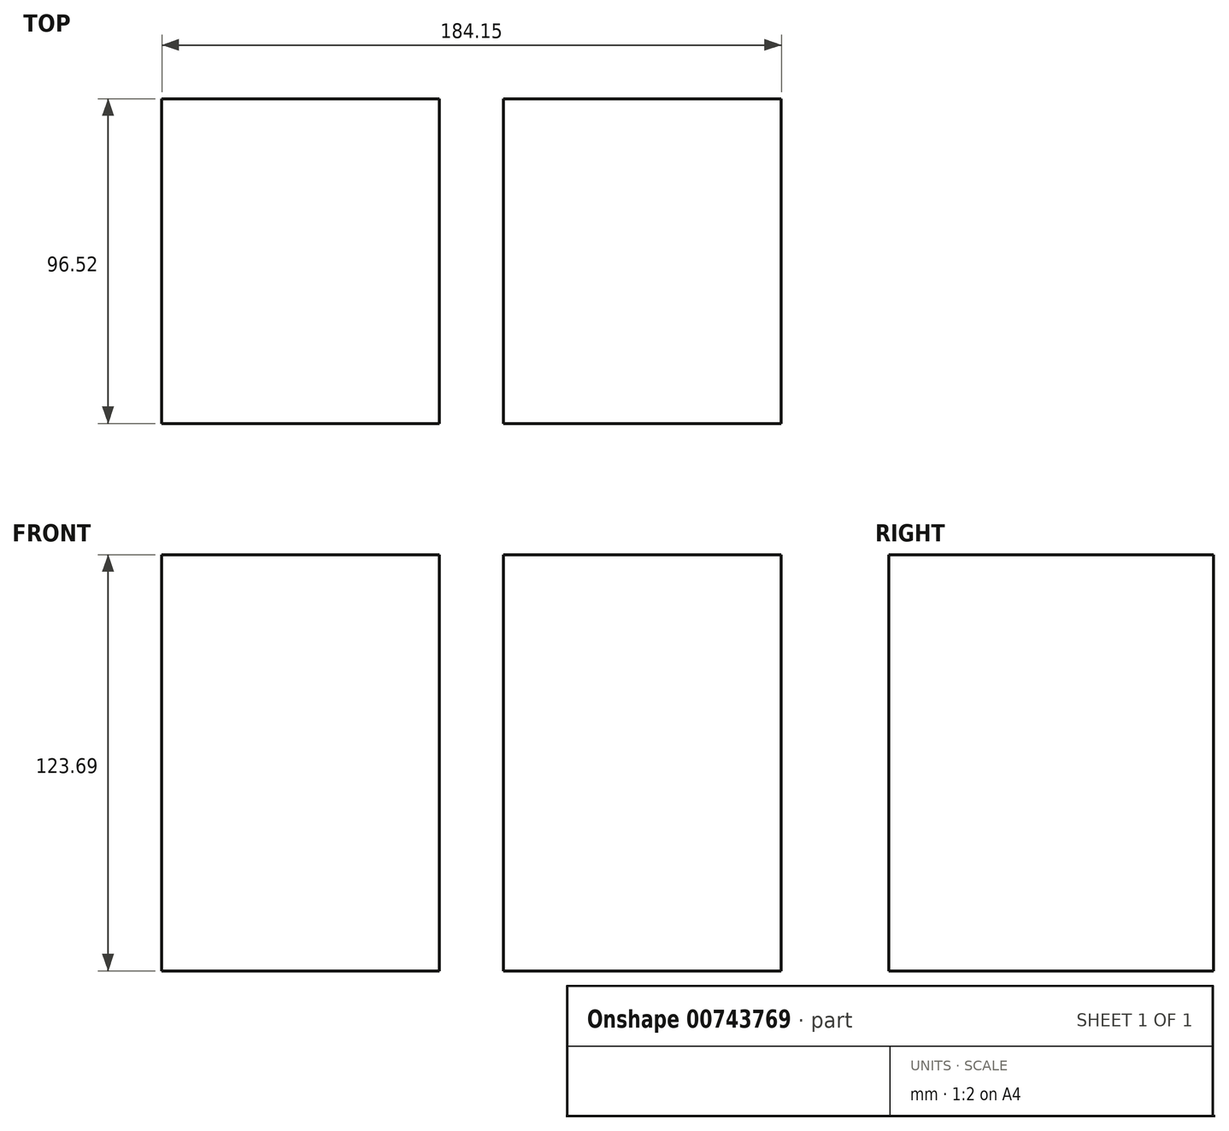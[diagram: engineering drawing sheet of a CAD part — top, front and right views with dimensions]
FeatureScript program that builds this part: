
annotation { "Feature Type Name" : "Feature", "Feature Type Description" : "" }
export const myFeature = defineFeature(function(context is Context, id is Id, definition is map)
    precondition{}
    {
        {
            var Q0;
            Q0=qCreatedBy(makeId("Front.planeOp"),FACE);
            var sketch = newSketch(context, id + "F0", { "sketchPlane" : qUnion([Q0])});
            skLineSegment(sketch, "E0.bottom", {"start": v(-0.21, 120.26) * mm, "end": v(82.34, 120.26) * mm});
            skLineSegment(sketch, "E0.top", {"start": v(-0.21, -3.43) * mm, "end": v(82.34, -3.43) * mm});
            skLineSegment(sketch, "E0.left", {"start": v(-0.21, 120.26) * mm, "end": v(-0.21, -3.43) * mm});
            skLineSegment(sketch, "E0.right", {"start": v(82.34, 120.26) * mm, "end": v(82.34, -3.43) * mm});
            skSolve(sketch);
        }
        {
            var Q0;
            Q0 = qSketchRegion(id + "F0", true);
            extrude(context, id + "F1", {"entities" : qUnion([Q0]), "oppositeDirection" : true, "depth" : 96.52 * mm, "offsetDistance" : 25 * mm});
        }
        {
            var Q0;
            Q0=makeQuery(id+"F1.opExtrude","SWEPT_BODY",BODY,{"disambiguationData":[OSD([sQuery(id+"F0.wireOp",EDGE,"E0.bottom"),sQuery(id+"F0.wireOp",EDGE,"E0.top"),sQuery(id+"F0.wireOp",EDGE,"E0.left"),sQuery(id+"F0.wireOp",EDGE,"E0.right")])]});
            transform(context, id + "F2", {"entities" : qUnion([Q0]), "transformType" : TransformType.TRANSLATION_3D, "dx" : 101.6 * mm, "dy" : 0 * mm, "dz" : 0 * mm, "makeCopy" : true});
        }
    });
